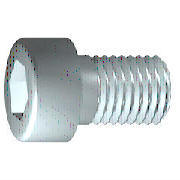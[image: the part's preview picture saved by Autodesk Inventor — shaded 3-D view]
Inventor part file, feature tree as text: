
AUTODESK INVENTOR PART (.ipt)
format: ipt  version: 2017 (Build 210142000, 142)  size: 194,560 bytes
history: native  units: mm (DEFAULTED — no unit token found)
features: sketch x2, extrude x1, plane x1, fillet x1
ambient origin geometry x7: Origin, YZ Plane, XY Plane, X Axis, Y Axis, Z Axis, Center Point
bodies: Solid1 (feature_tree), Body (feature_tree)
feature tree (5):
  extrude  "Slot"  Depth=6.0mm
  plane  "Work Plane1"
  fillet  "Fillet2"  Radius=6.0mm
  sketch  "Sketch1"  dims[d1=7.38655mm d2=0.61355mm d3=6.0mm]
  sketch  "Sketch2"  dims[d4=3.0mm d5=60.0deg d6=6.0mm d7=6.0mm d8=5.773503mm d9=10.0mm d10=90.0deg d11=10.0mm d12=0.0mm d13=7.38655mm d14=0.0mm d15=0.61345mm d16=0.61345mm d17=0.6mm d19=0.0mm d26=10.0mm d27=45.0deg d28=0.0mm d29=0.0mm d30=0.1mm]
